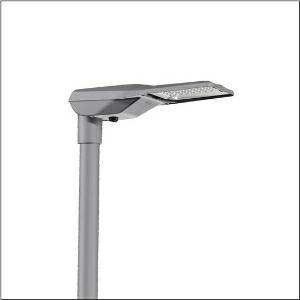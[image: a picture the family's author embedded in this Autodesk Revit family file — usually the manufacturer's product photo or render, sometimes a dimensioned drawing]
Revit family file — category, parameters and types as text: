
# Revit family: streetlight_sl_21_iq_mini___st1_0ab_5xe2m31u08hb_6af5
name_source: partatom
category: Lighting Fixtures
units: mm (PartAtom-declared; Revit-internal decimal feet)

## family parameters
Cut with Voids When Loaded = No
Host = Face
Light Source = No
Part Type = Normal
Room Calculation Point = No
Round Connector Dimension = Use Diameter
Shared = No

## types (1)
- --- (1 x LED, 8580 lm, 71 W, 3000K)
    Apparent Load = 71 VA
    CIE Flux Codes = 38 73 97 100 100
    Color Rendering = 70
    Color Temperature = 3000K
    Default Elevation = 1800 mm
    Description = Streetlight SL 21 iQ mini, mast luminaire, primary light control with lens, of PMMA, primary optical cover: cover, of toughened safety glass, transparent, light distribution: ST1.0aB, light emission: direct distribution, primary light characteristic: asymmetric, installation type: post-top, side-entry, LED, High Power LED, rated luminous flux: 8.580lm, luminous efficacy: 121lm/W, light colour: 730, colour temperature: 3000K, control gear: iQ-Street Remote, D4i with power reduction, control: pre-setting: logarithmic dimming characteristic, Street-Remote, Auto-Match, Temp-Guard, Lumen-Switch, Night-Set, Smart-Wire, Light-Fading, Desk-Remote (wireless, voltage-free reading and setting of iQ features in the workshop via application-optimized NFC function/RFID function), optimised constant luminous flux control (CLO 2.0), mains connection: 220..240V, AC, 50/60Hz, start of lifetime: 71W, end of service life: 75W, reduction: 30W, luminaire housing, of diecast aluminium, powder-coated, SITECO metallic grey (DB 702S), corrosivity category C5 high according to DIN EN ISO 12944, please order mast flange separately, inclination adjustable: 0°, 5°, 10°, 15°, sealing non-destructively replaceable, multi-level sealing system, length: 628mm, width: 235mm, height: 110mm, mast flange for spigot size: 42mm (side-entry): 5XC10008XM4, 60/48mm (side-entry/post-top): 5XC10108XM2, 76/60mm (side-entry/post-top): 5XC10108XM1, mounting height: 4..8m, Smart Interface below, protection rating (complete): IP66, insulation class (complete): insulation class II (safety insulation), certification: CE, ENEC, ENEC+, VDE, impact resistance: IK10, permissible operating ambient temperature for outdoor applications: -40..+50°C, standard-compliant lighting for roads and squares, packaging unit: 1 piece

Light Distribution: ST1.0aB
    Height = 110 mm
    Lamp = 1 x LED
    Lamp Light Flux = 8580 lm
    Lamp Power = 71 W
    Lamp count = 1
    Length = 625 mm
    Luminous efficacy = 121 lm/W
    Manufacturer = Siteco
    ModVariant = No
    Model = 5XE2M31U08HB
    Number of Poles = 1
    OnlyDefault = Yes
    Power Factor = 1
    Product Name = Streetlight SL 21 iQ mini | ST1.0aB
    Product group = mast luminaire | pylon top
    ProductGroupID = 6100
    Protection Class = Protection class II
    Protection Degree = IP 66
    RLX_Detail_Level = 1
    RLX_Emergency_Light_Flux = 0 lm
    RLX_Emergency_Type = 0
    RLX_Emergency_Type_DB = No
    RlxData = <blob elided: 92477 chars, md5=765756a0>
    Socket = socket
    Standby Power = 0 W
    System Light Flux = 8580 lm
    System Power = 71 W
    Type Comments = factory setting: luminous flux: 100 % | dim-lin: 254 | 716 mA
    Type Image = l_1003516.jpg
    URL = http://relux.com
    VarID = @adj_112547
    Voltage = 0 V
    Weight = 0.00 kg
    Width = 234 mm

## geometry (parser evidence)
native form markers: Blend x4, Sweep x11
no freeform markers — native parametric forms only
